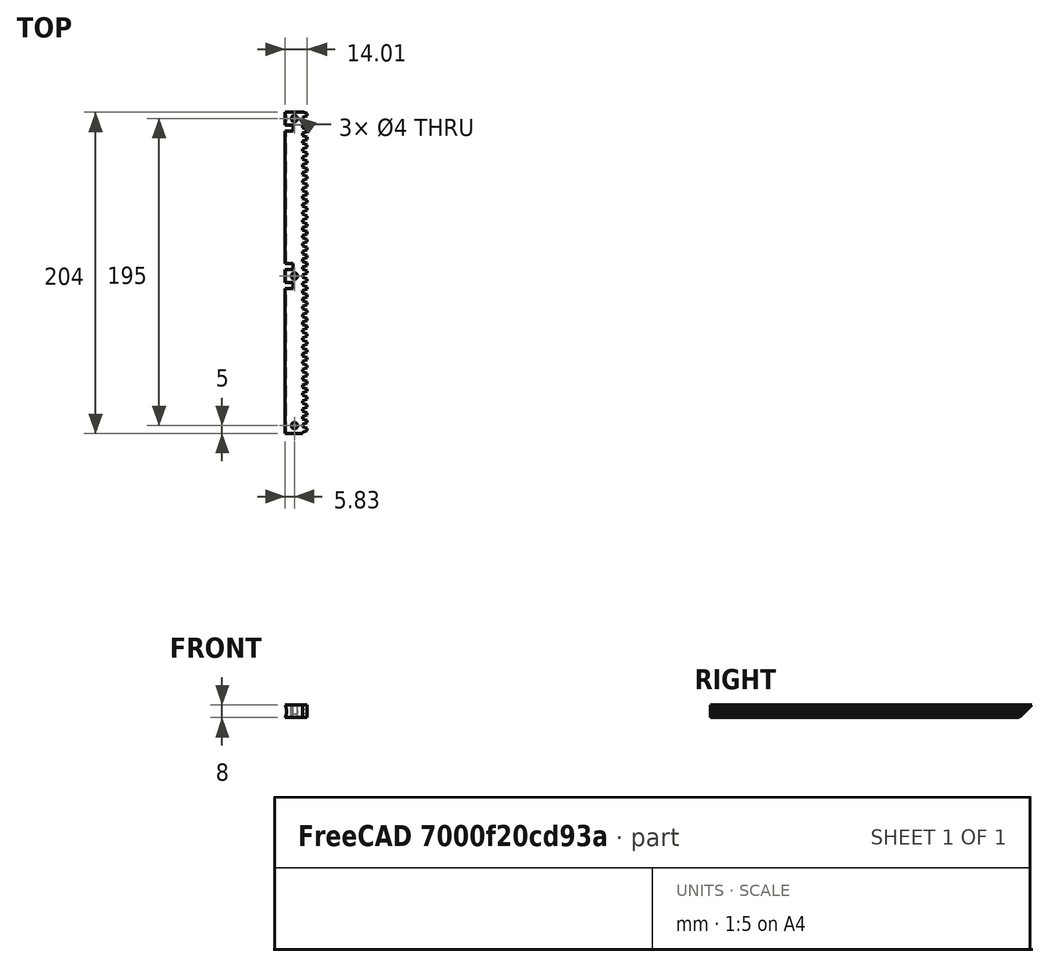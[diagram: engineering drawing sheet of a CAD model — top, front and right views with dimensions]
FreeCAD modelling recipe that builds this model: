
FCSTD DOCUMENT  (FreeCAD 0.17R13522 (Git))
Label: rack-end
License: All rights reserved
LicenseURL: http://en.wikipedia.org/wiki/All_rights_reserved
objects: Part::Box×5, Part::Cylinder×4, Part::MultiFuse×2, Part::FeaturePython×1, Part::Cut×1
note: 13 computed .brp shape members not serialized (recipe doc carries the construction recipe); baked Part::Feature solids carry a one-line shape summary decoded from their .brp

FEATURE [Part::FeaturePython] InvoluteRack  # WARN: FeaturePython — macro-defined, semantics opaque (R4)
  Placement = pos=(11.5915,2.5,-4) rot=(0,0,1;0rad)
  beta = 0
  double_helix = false
  head = 0
  height = 8
  module = 1.59155
  pressure_angle = 20
  teeth = 41
  thickness = 1
  expr: Placement.Base.x = 10 + 5 / pi
  expr: module = 5 / pi
FEATURE [Part::Box] Box  label="Cube"
  AttacherType = Attacher::AttachEngine3D
  Height = 8
  Length = 12
  Placement = pos=(-2,0,-4) rot=(0,0,1;0rad)
  Width = 205
FEATURE [Part::Cylinder] Cylinder
  Angle = 360
  AttacherType = Attacher::AttachEngine3D
  Height = 10
  Placement = pos=(5,5,-5) rot=(0,0,1;0rad)
  Radius = 2
FEATURE [Part::Cylinder] Cylinder001
  Angle = 360
  AttacherType = Attacher::AttachEngine3D
  Height = 10
  Placement = pos=(5,100,-5) rot=(0,0,1;0rad)
  Radius = 2
FEATURE [Part::Cylinder] Cylinder002
  Angle = 360
  AttacherType = Attacher::AttachEngine3D
  Height = 10
  Placement = pos=(5,200,-5) rot=(0,0,1;0rad)
  Radius = 2
FEATURE [Part::MultiFuse] Fusion  label="Positive Fusion"
  Shapes = -> [Box,InvoluteRack]
FEATURE [Part::Cylinder] Cylinder003  label="Rail"
  Angle = 360
  AttacherType = Attacher::AttachEngine3D
  Height = 210
  Placement = pos=(-10,0,0) rot=(-1,0,0;1.5708rad)
  Radius = 10
FEATURE [Part::Box] Box002  label="Cube002"
  AttacherType = Attacher::AttachEngine3D
  Height = 20
  Length = 20
  Placement = pos=(-5,195,-5) rot=(-1,0,0;0.785398rad)
  Width = 10
FEATURE [Part::Box] Box003  label="Cube003"
  AttacherType = Attacher::AttachEngine3D
  Height = 8
  Length = 5
  Placement = pos=(-1,92,-4) rot=(0,0,1;0rad)
  Width = 4
FEATURE [Part::Box] Box005  label="Cube005"
  AttacherType = Attacher::AttachEngine3D
  Height = 8
  Length = 5
  Placement = pos=(-1,192,-4) rot=(0,0,1;0rad)
  Width = 4
FEATURE [Part::Box] Box004  label="Cube004"
  AttacherType = Attacher::AttachEngine3D
  Height = 8
  Length = 5
  Placement = pos=(-1,104,-4) rot=(0,0,1;0rad)
  Width = 4
FEATURE [Part::MultiFuse] Fusion001  label="Negative Fusion"
  Shapes = -> [Cylinder,Cylinder001,Cylinder002,Cylinder003,Box002,Box003,Box005,Box004]
FEATURE [Part::Cut] Cut
  Base = -> Fusion
  Tool = -> Fusion001
